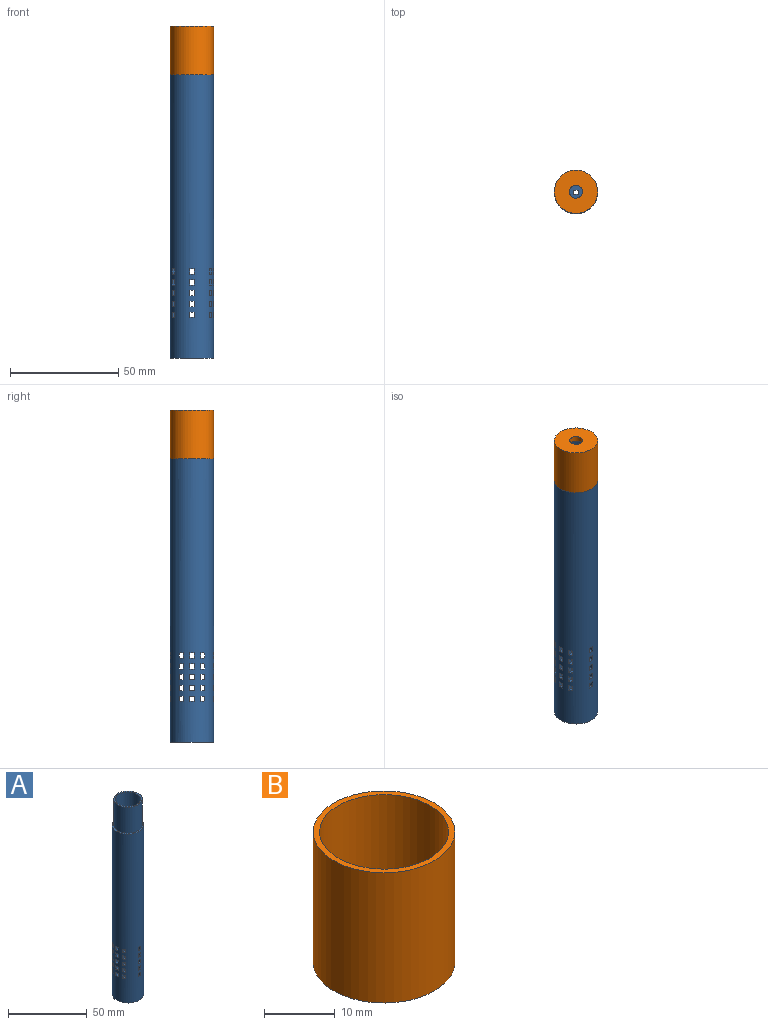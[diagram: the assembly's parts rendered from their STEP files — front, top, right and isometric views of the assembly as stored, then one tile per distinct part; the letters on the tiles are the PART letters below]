
ASSEMBLY  parts=2 mates=1
PART A: 203 faces, bbox 20x20x151 mm
  f0: plane 18x18mm, normal (0,0,1), area 53.4mm2, adj f163,f201
  f1: cylinder r=10mm len=131mm, axis (0,0,1), area 8014.7mm2, adj f2,f3,f4,f5,f6,f7,f8,f9
  f2: plane 20x20mm, normal (0,0,-1), area 278.2mm2, adj f1,f165,f166,f167,f168,f169,f170,f171
  f3: plane 2.06x2mm, normal (0,0,1), area 4mm2, adj f1,f31,f116,f163
  f4: plane 2.06x2mm, normal (0,0,-1), area 4mm2, adj f1,f31,f116,f163
  f5: plane 2.06x2mm, normal (0,0,-1), area 4mm2, adj f1,f36,f125,f163
  f6: plane 2.06x2mm, normal (0,0,1), area 4mm2, adj f1,f36,f125,f163
  f7: plane 2.06x2mm, normal (0,0,-1), area 4mm2, adj f1,f37,f131,f163
  f8: plane 2.06x2mm, normal (0,0,1), area 4mm2, adj f1,f37,f131,f163
  f9: plane 2.06x2mm, normal (0,0,1), area 4mm2, adj f1,f38,f138,f163
  f10: plane 2.06x2mm, normal (0,0,-1), area 4mm2, adj f1,f38,f138,f163
  f11: plane 2.06x2mm, normal (0,0,1), area 4mm2, adj f1,f43,f144,f163
  f12: plane 2.06x2mm, normal (0,0,-1), area 4mm2, adj f1,f43,f144,f163
  f13: plane 2.06x2mm, normal (0,0,-1), area 4mm2, adj f1,f48,f153,f163
  f14: plane 2.06x2mm, normal (0,0,1), area 4mm2, adj f1,f48,f153,f163
  f15: plane 2.06x2mm, normal (0,0,-1), area 4mm2, adj f1,f49,f154,f163
  f16: plane 2.06x2mm, normal (0,0,1), area 4mm2, adj f1,f49,f154,f163
  f17: plane 2.06x2mm, normal (0,0,-1), area 4mm2, adj f1,f50,f155,f163
  f18: plane 2.06x2mm, normal (0,0,1), area 4mm2, adj f1,f50,f155,f163
  f19: plane 2.06x2mm, normal (0,0,-1), area 4mm2, adj f1,f51,f156,f163
  f20: plane 2.06x2mm, normal (0,0,1), area 4mm2, adj f1,f51,f156,f163
  f21: plane 2.06x2mm, normal (0,0,-1), area 4mm2, adj f1,f52,f157,f163
  f22: plane 2.06x2mm, normal (0,0,1), area 4mm2, adj f1,f52,f157,f163
  f23: plane 3.87x2mm, normal (0,0,-1), area 4.9mm2, adj f1,f24,f26,f163
  f24: plane 2.71x2.5mm, normal (0,-1,0), area 6.8mm2, adj f1,f23,f25,f163
  f25: plane 3.87x2mm, normal (0,0,1), area 4.9mm2, adj f1,f24,f26,f163
  f26: plane 2.5x2.24mm, normal (0,1,0), area 5.6mm2, adj f1,f23,f25,f163
  f27: plane 2.5x2.24mm, normal (0,1,0), area 5.6mm2, adj f1,f29,f30,f163
  f28: plane 2.71x2.5mm, normal (0,-1,0), area 6.8mm2, adj f1,f29,f30,f163
  f29: plane 3.87x2mm, normal (0,0,1), area 4.9mm2, adj f1,f27,f28,f163
  f30: plane 3.87x2mm, normal (0,0,-1), area 4.9mm2, adj f1,f27,f28,f163
  f31: plane 2.5x2.01mm, normal (0,-1,0), area 5mm2, adj f1,f3,f4,f163
  f32: plane 2.71x2.5mm, normal (0,-1,0), area 6.8mm2, adj f1,f33,f35,f163
  f33: plane 3.87x2mm, normal (0,0,1), area 4.9mm2, adj f1,f32,f34,f163
  f34: plane 2.5x2.24mm, normal (0,1,0), area 5.6mm2, adj f1,f33,f35,f163
  f35: plane 3.87x2mm, normal (0,0,-1), area 4.9mm2, adj f1,f32,f34,f163
  f36: plane 2.5x2.01mm, normal (0,-1,0), area 5mm2, adj f1,f5,f6,f163
  f37: plane 2.5x2.01mm, normal (0,-1,0), area 5mm2, adj f1,f7,f8,f163
  f38: plane 2.5x2.01mm, normal (0,-1,0), area 5mm2, adj f1,f9,f10,f163
  f39: plane 3.87x2mm, normal (0,0,1), area 4.9mm2, adj f1,f40,f42,f163
  f40: plane 2.71x2.5mm, normal (0,-1,0), area 6.8mm2, adj f1,f39,f41,f163
  f41: plane 3.87x2mm, normal (0,0,-1), area 4.9mm2, adj f1,f40,f42,f163
  f42: plane 2.5x2.24mm, normal (0,1,0), area 5.6mm2, adj f1,f39,f41,f163
  f43: plane 2.5x2.01mm, normal (0,-1,0), area 5mm2, adj f1,f11,f12,f163
  f44: plane 3.87x2mm, normal (0,0,-1), area 4.9mm2, adj f1,f45,f47,f163
  f45: plane 2.5x2.24mm, normal (0,1,0), area 5.6mm2, adj f1,f44,f46,f163
  f46: plane 3.87x2mm, normal (0,0,1), area 4.9mm2, adj f1,f45,f47,f163
  f47: plane 2.71x2.5mm, normal (0,-1,0), area 6.8mm2, adj f1,f44,f46,f163
  f48: plane 2.5x2.01mm, normal (1,0,0), area 5mm2, adj f1,f13,f14,f163
  f49: plane 2.5x2.01mm, normal (1,0,0), area 5mm2, adj f1,f15,f16,f163
  f50: plane 2.5x2.01mm, normal (1,0,0), area 5mm2, adj f1,f17,f18,f163
  f51: plane 2.5x2.01mm, normal (1,0,0), area 5mm2, adj f1,f19,f20,f163
  f52: plane 2.5x2.01mm, normal (1,0,0), area 5mm2, adj f1,f21,f22,f163
  f53: plane 2.06x2mm, normal (0,0,-1), area 4mm2, adj f1,f77,f115,f163
  f54: plane 2.06x2mm, normal (0,0,1), area 4mm2, adj f1,f77,f115,f163
  f55: plane 2.06x2mm, normal (0,0,1), area 4mm2, adj f1,f82,f126,f163
  f56: plane 2.06x2mm, normal (0,0,-1), area 4mm2, adj f1,f82,f126,f163
  f57: plane 2.06x2mm, normal (0,0,1), area 4mm2, adj f1,f87,f132,f163
  f58: plane 2.06x2mm, normal (0,0,-1), area 4mm2, adj f1,f87,f132,f163
  f59: plane 2.06x2mm, normal (0,0,-1), area 4mm2, adj f1,f92,f137,f163
  f60: plane 2.06x2mm, normal (0,0,1), area 4mm2, adj f1,f92,f137,f163
  f61: plane 2.06x2mm, normal (0,0,-1), area 4mm2, adj f1,f93,f143,f163
  f62: plane 2.06x2mm, normal (0,0,1), area 4mm2, adj f1,f93,f143,f163
  f63: plane 2.06x2mm, normal (0,0,1), area 4mm2, adj f1,f98,f158,f163
  f64: plane 2.06x2mm, normal (0,0,-1), area 4mm2, adj f1,f98,f158,f163
  f65: plane 2.06x2mm, normal (0,0,1), area 4mm2, adj f1,f99,f159,f163
  f66: plane 2.06x2mm, normal (0,0,-1), area 4mm2, adj f1,f99,f159,f163
  f67: plane 2.06x2mm, normal (0,0,1), area 4mm2, adj f1,f100,f160,f163
  f68: plane 2.06x2mm, normal (0,0,-1), area 4mm2, adj f1,f100,f160,f163
  f69: plane 2.06x2mm, normal (0,0,1), area 4mm2, adj f1,f101,f161,f163
  f70: plane 2.06x2mm, normal (0,0,-1), area 4mm2, adj f1,f101,f161,f163
  f71: plane 2.06x2mm, normal (0,0,1), area 4mm2, adj f1,f102,f162,f163
  f72: plane 2.06x2mm, normal (0,0,-1), area 4mm2, adj f1,f102,f162,f163
  f73: plane 3.87x2mm, normal (0,0,1), area 4.9mm2, adj f1,f75,f76,f163
  f74: plane 3.87x2mm, normal (0,0,-1), area 4.9mm2, adj f1,f75,f76,f163
  f75: plane 2.5x2.24mm, normal (0,-1,0), area 5.6mm2, adj f1,f73,f74,f163
  f76: plane 2.71x2.5mm, normal (0,1,0), area 6.8mm2, adj f1,f73,f74,f163
  f77: plane 2.5x2.01mm, normal (0,1,0), area 5mm2, adj f1,f53,f54,f163
  f78: plane 2.5x2.24mm, normal (0,-1,0), area 5.6mm2, adj f1,f79,f81,f163
  f79: plane 3.87x2mm, normal (0,0,-1), area 4.9mm2, adj f1,f78,f80,f163
  f80: plane 2.71x2.5mm, normal (0,1,0), area 6.8mm2, adj f1,f79,f81,f163
  f81: plane 3.87x2mm, normal (0,0,1), area 4.9mm2, adj f1,f78,f80,f163
  f82: plane 2.5x2.01mm, normal (0,1,0), area 5mm2, adj f1,f55,f56,f163
  f83: plane 3.87x2mm, normal (0,0,1), area 4.9mm2, adj f1,f84,f86,f163
  f84: plane 2.5x2.24mm, normal (0,-1,0), area 5.6mm2, adj f1,f83,f85,f163
  f85: plane 3.87x2mm, normal (0,0,-1), area 4.9mm2, adj f1,f84,f86,f163
  f86: plane 2.71x2.5mm, normal (0,1,0), area 6.8mm2, adj f1,f83,f85,f163
  f87: plane 2.5x2.01mm, normal (0,1,0), area 5mm2, adj f1,f57,f58,f163
  f88: plane 3.89x2.02mm, normal (0,0,1), area 4.9mm2, adj f1,f89,f91,f163
  f89: plane 2.5x2.24mm, normal (0,-1,0), area 5.6mm2, adj f1,f88,f90,f163
  f90: plane 3.89x2.02mm, normal (0,0,-1), area 4.9mm2, adj f1,f89,f91,f163
  f91: plane 2.71x2.5mm, normal (0,1,0), area 6.8mm2, adj f1,f88,f90,f163
  f92: plane 2.5x2.01mm, normal (0,1,0), area 5mm2, adj f1,f59,f60,f163
  f93: plane 2.5x2.01mm, normal (0,1,0), area 5mm2, adj f1,f61,f62,f163
  f94: plane 2.5x2.24mm, normal (0,-1,0), area 5.6mm2, adj f1,f95,f97,f163
  f95: plane 3.87x2mm, normal (0,0,-1), area 4.9mm2, adj f1,f94,f96,f163
  f96: plane 2.71x2.5mm, normal (0,1,0), area 6.8mm2, adj f1,f95,f97,f163
  f97: plane 3.87x2mm, normal (0,0,1), area 4.9mm2, adj f1,f94,f96,f163
  f98: plane 2.5x2.01mm, normal (-1,0,0), area 5mm2, adj f1,f63,f64,f163
  f99: plane 2.5x2.01mm, normal (-1,0,0), area 5mm2, adj f1,f65,f66,f163
  f100: plane 2.5x2.01mm, normal (-1,0,0), area 5mm2, adj f1,f67,f68,f163
  f101: plane 2.5x2.01mm, normal (-1,0,0), area 5mm2, adj f1,f69,f70,f163
  f102: plane 2.5x2.01mm, normal (-1,0,0), area 5mm2, adj f1,f71,f72,f163
  f103: plane 2.5x2.24mm, normal (0,1,0), area 5.6mm2, adj f1,f104,f106,f163
  f104: plane 3.87x2mm, normal (0,0,1), area 4.9mm2, adj f1,f103,f105,f163
  f105: plane 2.71x2.5mm, normal (0,-1,0), area 6.8mm2, adj f1,f104,f106,f163
  f106: plane 3.87x2mm, normal (0,0,-1), area 4.9mm2, adj f1,f103,f105,f163
  f107: plane 3.87x2mm, normal (0,0,-1), area 4.9mm2, adj f1,f108,f110,f163
  f108: plane 2.71x2.5mm, normal (0,1,0), area 6.8mm2, adj f1,f107,f109,f163
  f109: plane 3.87x2mm, normal (0,0,1), area 4.9mm2, adj f1,f108,f110,f163
  f110: plane 2.5x2.24mm, normal (0,-1,0), area 5.6mm2, adj f1,f107,f109,f163
  f111: plane 2.71x2.5mm, normal (0,-1,0), area 6.8mm2, adj f1,f112,f114,f163
  f112: plane 3.87x2mm, normal (0,0,-1), area 4.9mm2, adj f1,f111,f113,f163
  f113: plane 2.5x2.24mm, normal (0,1,0), area 5.6mm2, adj f1,f112,f114,f163
  f114: plane 3.87x2mm, normal (0,0,1), area 4.9mm2, adj f1,f111,f113,f163
  f115: plane 2.5x2.01mm, normal (0,-1,0), area 5mm2, adj f1,f53,f54,f163
  f116: plane 2.5x2.01mm, normal (0,1,0), area 5mm2, adj f1,f3,f4,f163
  f117: plane 3.87x2mm, normal (0,0,1), area 4.9mm2, adj f1,f118,f120,f163
  f118: plane 2.71x2.5mm, normal (0,1,0), area 6.8mm2, adj f1,f117,f119,f163
  f119: plane 3.87x2mm, normal (0,0,-1), area 4.9mm2, adj f1,f118,f120,f163
  f120: plane 2.5x2.24mm, normal (0,-1,0), area 5.6mm2, adj f1,f117,f119,f163
  f121: plane 3.87x2mm, normal (0,0,-1), area 4.9mm2, adj f1,f122,f124,f163
  f122: plane 2.5x2.24mm, normal (0,1,0), area 5.6mm2, adj f1,f121,f123,f163
  f123: plane 3.87x2mm, normal (0,0,1), area 4.9mm2, adj f1,f122,f124,f163
  f124: plane 2.71x2.5mm, normal (0,-1,0), area 6.8mm2, adj f1,f121,f123,f163
  f125: plane 2.5x2.01mm, normal (0,1,0), area 5mm2, adj f1,f5,f6,f163
  f126: plane 2.5x2.01mm, normal (0,-1,0), area 5mm2, adj f1,f55,f56,f163
  f127: plane 2.71x2.5mm, normal (0,1,0), area 6.8mm2, adj f1,f128,f130,f163
  f128: plane 3.87x2mm, normal (0,0,-1), area 4.9mm2, adj f1,f127,f129,f163
  f129: plane 2.5x2.24mm, normal (0,-1,0), area 5.6mm2, adj f1,f128,f130,f163
  f130: plane 3.87x2mm, normal (0,0,1), area 4.9mm2, adj f1,f127,f129,f163
  f131: plane 2.5x2.01mm, normal (0,1,0), area 5mm2, adj f1,f7,f8,f163
  f132: plane 2.5x2.01mm, normal (0,-1,0), area 5mm2, adj f1,f57,f58,f163
  f133: plane 2.71x2.5mm, normal (0,1,0), area 6.8mm2, adj f1,f134,f136,f163
  f134: plane 3.89x2.02mm, normal (0,0,-1), area 4.9mm2, adj f1,f133,f135,f163
  f135: plane 2.5x2.24mm, normal (0,-1,0), area 5.6mm2, adj f1,f134,f136,f163
  f136: plane 3.89x2.02mm, normal (0,0,1), area 4.9mm2, adj f1,f133,f135,f163
  f137: plane 2.5x2.01mm, normal (0,-1,0), area 5mm2, adj f1,f59,f60,f163
  f138: plane 2.5x2.01mm, normal (0,1,0), area 5mm2, adj f1,f9,f10,f163
  f139: plane 2.5x2.24mm, normal (0,1,0), area 5.6mm2, adj f1,f140,f142,f163
  f140: plane 3.87x2mm, normal (0,0,-1), area 4.9mm2, adj f1,f139,f141,f163
  f141: plane 2.71x2.5mm, normal (0,-1,0), area 6.8mm2, adj f1,f140,f142,f163
  f142: plane 3.87x2mm, normal (0,0,1), area 4.9mm2, adj f1,f139,f141,f163
  f143: plane 2.5x2.01mm, normal (0,-1,0), area 5mm2, adj f1,f61,f62,f163
  f144: plane 2.5x2.01mm, normal (0,1,0), area 5mm2, adj f1,f11,f12,f163
  f145: plane 3.87x2mm, normal (0,0,1), area 4.9mm2, adj f1,f146,f148,f163
  f146: plane 2.71x2.5mm, normal (0,1,0), area 6.8mm2, adj f1,f145,f147,f163
  f147: plane 3.87x2mm, normal (0,0,-1), area 4.9mm2, adj f1,f146,f148,f163
  f148: plane 2.5x2.24mm, normal (0,-1,0), area 5.6mm2, adj f1,f145,f147,f163
  f149: plane 3.87x2mm, normal (0,0,1), area 4.9mm2, adj f1,f151,f152,f163
  f150: plane 3.87x2mm, normal (0,0,-1), area 4.9mm2, adj f1,f151,f152,f163
  f151: plane 2.71x2.5mm, normal (0,-1,0), area 6.8mm2, adj f1,f149,f150,f163
  f152: plane 2.5x2.24mm, normal (0,1,0), area 5.6mm2, adj f1,f149,f150,f163
  f153: plane 2.5x2.01mm, normal (-1,0,0), area 5mm2, adj f1,f13,f14,f163
  f154: plane 2.5x2.01mm, normal (-1,0,0), area 5mm2, adj f1,f15,f16,f163
  f155: plane 2.5x2.01mm, normal (-1,0,0), area 5mm2, adj f1,f17,f18,f163
  f156: plane 2.5x2.01mm, normal (-1,0,0), area 5mm2, adj f1,f19,f20,f163
  f157: plane 2.5x2.01mm, normal (-1,0,0), area 5mm2, adj f1,f21,f22,f163
  f158: plane 2.5x2.01mm, normal (1,0,0), area 5mm2, adj f1,f63,f64,f163
  f159: plane 2.5x2.01mm, normal (1,0,0), area 5mm2, adj f1,f65,f66,f163
  f160: plane 2.5x2.01mm, normal (1,0,0), area 5mm2, adj f1,f67,f68,f163
  f161: plane 2.5x2.01mm, normal (1,0,0), area 5mm2, adj f1,f69,f70,f163
  f162: plane 2.5x2.01mm, normal (1,0,0), area 5mm2, adj f1,f71,f72,f163
  f163: cylinder r=8mm len=149mm, axis (0,0,-1), area 7259.4mm2, adj f0,f3,f4,f5,f6,f7,f8,f9
  f164: plane 16x16mm, normal (0,0,1), area 165.1mm2, adj f163,f165,f166,f167,f168,f169,f170,f171
  f165: plane 2x2mm, normal (0,1,0), area 4mm2, adj f2,f164,f166,f168
  f166: plane 2x2mm, normal (-1,0,0), area 4mm2, adj f2,f164,f165,f167
  f167: plane 2x2mm, normal (0,-1,0), area 4mm2, adj f2,f164,f166,f168
  f168: plane 2x2mm, normal (1,0,0), area 4mm2, adj f2,f164,f165,f167
  f169: plane 2x2mm, normal (0,-1,0), area 4mm2, adj f2,f164,f170,f172
  f170: plane 2x2mm, normal (1,0,0), area 4mm2, adj f2,f164,f169,f171
  f171: plane 2x2mm, normal (0,1,0), area 4mm2, adj f2,f164,f170,f172
  f172: plane 2x2mm, normal (-1,0,0), area 4mm2, adj f2,f164,f169,f171
  f173: plane 2x2mm, normal (0,1,0), area 4mm2, adj f2,f164,f174,f176
  f174: plane 2x2mm, normal (-1,0,0), area 4mm2, adj f2,f164,f173,f175
  f175: plane 2x2mm, normal (0,-1,0), area 4mm2, adj f2,f164,f174,f176
  f176: plane 2x2mm, normal (1,0,0), area 4mm2, adj f2,f164,f173,f175
  f177: plane 2x2mm, normal (0,1,0), area 4mm2, adj f2,f164,f178,f180
  f178: plane 2x2mm, normal (-1,0,0), area 4mm2, adj f2,f164,f177,f179
  f179: plane 2x2mm, normal (0,-1,0), area 4mm2, adj f2,f164,f178,f180
  f180: plane 2x2mm, normal (1,0,0), area 4mm2, adj f2,f164,f177,f179
  f181: plane 2x2mm, normal (1,0,0), area 4mm2, adj f2,f164,f182,f184
  f182: plane 2x2mm, normal (0,1,0), area 4mm2, adj f2,f164,f181,f183
  f183: plane 2x2mm, normal (-1,0,0), area 4mm2, adj f2,f164,f182,f184
  f184: plane 2x2mm, normal (0,-1,0), area 4mm2, adj f2,f164,f181,f183
  f185: plane 2x2mm, normal (0,1,0), area 4mm2, adj f2,f164,f186,f188
  f186: plane 2x2mm, normal (-1,0,0), area 4mm2, adj f2,f164,f185,f187
  f187: plane 2x2mm, normal (0,-1,0), area 4mm2, adj f2,f164,f186,f188
  f188: plane 2x2mm, normal (1,0,0), area 4mm2, adj f2,f164,f185,f187
  f189: plane 2x2mm, normal (1,0,0), area 4mm2, adj f2,f164,f190,f192
  f190: plane 2x2mm, normal (0,1,0), area 4mm2, adj f2,f164,f189,f191
  f191: plane 2x2mm, normal (-1,0,0), area 4mm2, adj f2,f164,f190,f192
  f192: plane 2x2mm, normal (0,-1,0), area 4mm2, adj f2,f164,f189,f191
  f193: plane 2x2mm, normal (0,1,0), area 4mm2, adj f2,f164,f194,f196
  f194: plane 2x2mm, normal (-1,0,0), area 4mm2, adj f2,f164,f193,f195
  f195: plane 2x2mm, normal (0,-1,0), area 4mm2, adj f2,f164,f194,f196
  f196: plane 2x2mm, normal (1,0,0), area 4mm2, adj f2,f164,f193,f195
  f197: plane 2x2mm, normal (0,1,0), area 4mm2, adj f2,f164,f198,f200
  f198: plane 2x2mm, normal (-1,0,0), area 4mm2, adj f2,f164,f197,f199
  f199: plane 2x2mm, normal (0,-1,0), area 4mm2, adj f2,f164,f198,f200
  f200: plane 2x2mm, normal (1,0,0), area 4mm2, adj f2,f164,f197,f199
  f201: cylinder r=9mm len=20mm, axis (0,0,1), area 1131mm2, adj f0,f202
  f202: plane 20x20mm, normal (0,0,1), area 59.7mm2, adj f1,f201
PART B: 6 faces, bbox 20x20x22.5 mm
  f0: plane 18.2x18.2mm, normal (0,0,1), area 231.9mm2, adj f3,f4
  f1: cylinder r=10mm len=22.5mm, axis (0,0,-1), area 1413.7mm2, adj f2,f5
  f2: plane 20x20mm, normal (0,0,-1), area 285.9mm2, adj f1,f3
  f3: cylinder r=3mm len=6mm, axis (0,0,-1), area 47.1mm2, adj f0,f2
  f4: cylinder r=9.1mm len=20mm, axis (0,0,-1), area 1143.5mm2, adj f0,f5
  f5: plane 20x20mm, normal (0,0,1), area 54mm2, adj f1,f4
PLACE A t=(-48.36,3.53,-53.82)mm
PLACE B rot(axis=(1,0,0),180deg) t=(-48.36,3.53,99.68)mm
MATE fastened B.f1 <-> A.f163  axis (0,0,-1) through (-48.36,3.53,97.18)mm
